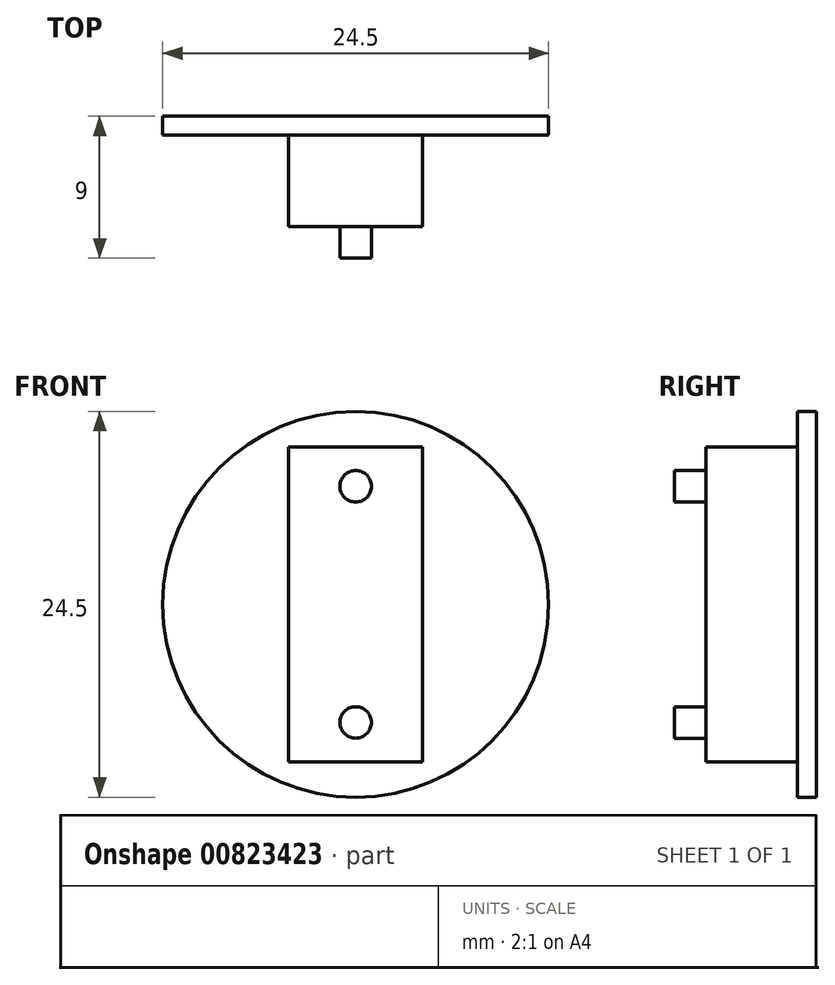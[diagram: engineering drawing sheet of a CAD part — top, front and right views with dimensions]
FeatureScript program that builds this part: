
annotation { "Feature Type Name" : "Feature", "Feature Type Description" : "" }
export const myFeature = defineFeature(function(context is Context, id is Id, definition is map)
    precondition{}
    {
        {
            var Q0;
            Q0=qCreatedBy(makeId("Front.planeOp"),FACE);
            var sketch = newSketch(context, id + "F0", { "sketchPlane" : qUnion([Q0])});
            skCircle(sketch, "E0", {"center": v(0, 0) * mm, "radius": 12.25 * mm});
            skCircle(sketch, "E1", {"center": v(0, 7.5) * mm, "radius": 1 * mm});
            skCircle(sketch, "E2", {"center": v(0, -7.5) * mm, "radius": 1 * mm});
            skLineSegment(sketch, "E3.bottom", {"start": v(4.25, 10) * mm, "end": v(-4.25, 10) * mm});
            skLineSegment(sketch, "E3.top", {"start": v(4.25, -10) * mm, "end": v(-4.25, -10) * mm});
            skLineSegment(sketch, "E3.left", {"start": v(4.25, 10) * mm, "end": v(4.25, -10) * mm});
            skLineSegment(sketch, "E3.right", {"start": v(-4.25, 10) * mm, "end": v(-4.25, -10) * mm});
            skSolve(sketch);
        }
        {
            var Q0;
            Q0=makeQuery(id+"F0.imprint","IMPRINT",FACE,{"disambiguationData":[TD([[makeQuery(id+"F0.imprint","IMPRINT",EDGE,{"derivedFrom":sQuery(id+"F0.wireOp",EDGE,"E0")}),1.0]])]});
            extrude(context, id + "F1", {"entities" : qUnion([Q0]), "depth" : 1.2 * mm, "offsetDistance" : 25 * mm});
        }
        {
            var Q0;
            Q0=makeQuery(id+"F0.imprint","IMPRINT",FACE,{"disambiguationData":[TD([[makeQuery(id+"F0.imprint","IMPRINT",EDGE,{"derivedFrom":sQuery(id+"F0.wireOp",EDGE,"E1")}),-1.0]])]});
            extrude(context, id + "F2", {"entities" : qUnion([Q0]), "operationType" : NewBodyOperationType.ADD, "depth" : 7 * mm, "offsetDistance" : 25 * mm});
        }
        {
            var Q0;
            Q0=makeQuery(id+"F0.imprint","IMPRINT",FACE,{"disambiguationData":[TD([[makeQuery(id+"F0.imprint","IMPRINT",EDGE,{"derivedFrom":sQuery(id+"F0.wireOp",EDGE,"E1")}),1.0]])]});
            var Q1;
            Q1=makeQuery(id+"F0.imprint","IMPRINT",FACE,{"disambiguationData":[TD([[makeQuery(id+"F0.imprint","IMPRINT",EDGE,{"derivedFrom":sQuery(id+"F0.wireOp",EDGE,"E2")}),1.0]])]});
            extrude(context, id + "F3", {"entities" : qUnion([Q0, Q1]), "operationType" : NewBodyOperationType.ADD, "depth" : 9 * mm, "offsetDistance" : 25 * mm});
        }
    });
